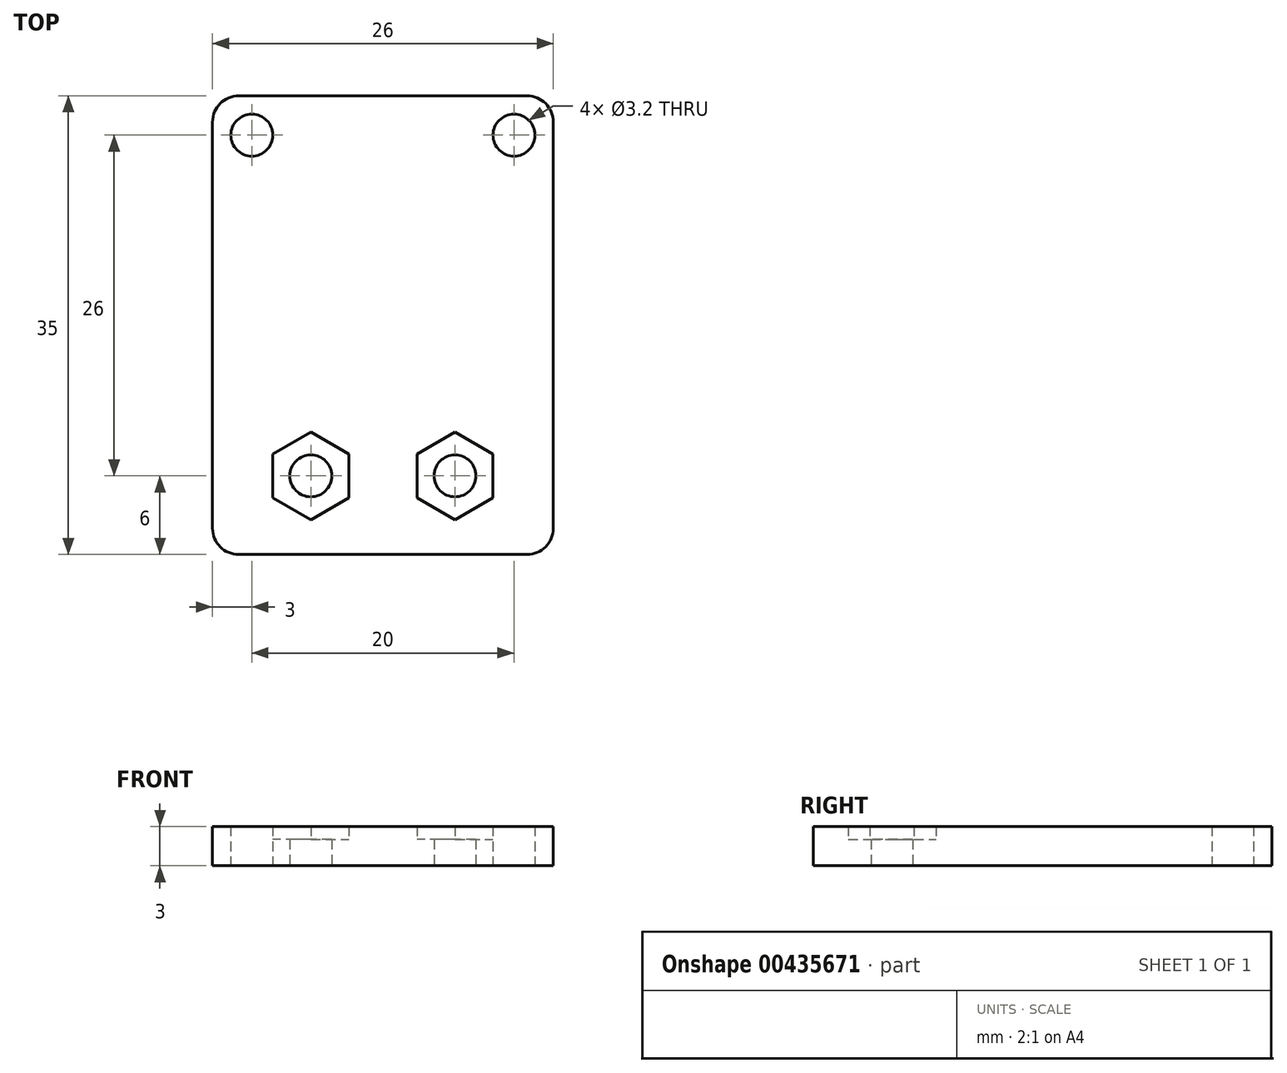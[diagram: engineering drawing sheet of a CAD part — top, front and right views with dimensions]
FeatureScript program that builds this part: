
annotation { "Feature Type Name" : "Feature", "Feature Type Description" : "" }
export const myFeature = defineFeature(function(context is Context, id is Id, definition is map)
    precondition{}
    {
        {
            var Q0;
            Q0=qCreatedBy(makeId("Top.planeOp"),FACE);
            var sketch = newSketch(context, id + "F0", { "sketchPlane" : qUnion([Q0])});
            skLineSegment(sketch, "E0.bottom", {"start": v(2, 0) * mm, "end": v(24, 0) * mm});
            skLineSegment(sketch, "E0.top", {"start": v(2, 35) * mm, "end": v(24, 35) * mm});
            skLineSegment(sketch, "E0.left", {"start": v(0, 2) * mm, "end": v(0, 33) * mm});
            skLineSegment(sketch, "E0.right", {"start": v(26, 2) * mm, "end": v(26, 33) * mm});
            skCircle(sketch, "E1", {"center": v(3, 32) * mm, "radius": 1.6 * mm});
            skCircle(sketch, "E2", {"center": v(23, 32) * mm, "radius": 1.6 * mm});
            skCircle(sketch, "E3", {"center": v(7.5, 6) * mm, "radius": 1.6 * mm});
            skCircle(sketch, "E4", {"center": v(18.5, 6) * mm, "radius": 1.6 * mm});
            skPoint(sketch, "E5.visualSharp", {"position": v(0, 35) * mm});
            skArc(sketch, "E5.filletArc", {"start": v(2, 35) * mm, "mid": v(0.59, 34.41) * mm, "end": v(0, 33) * mm});
            skPoint(sketch, "E6.visualSharp", {"position": v(26, 35) * mm});
            skArc(sketch, "E6.filletArc", {"start": v(26, 33) * mm, "mid": v(25.41, 34.41) * mm, "end": v(24, 35) * mm});
            skPoint(sketch, "E7.visualSharp", {"position": v(26, 0) * mm});
            skArc(sketch, "E7.filletArc", {"start": v(24, 0) * mm, "mid": v(25.41, 0.59) * mm, "end": v(26, 2) * mm});
            skPoint(sketch, "E8.visualSharp", {"position": v(0, 0) * mm});
            skArc(sketch, "E8.filletArc", {"start": v(0, 2) * mm, "mid": v(0.59, 0.59) * mm, "end": v(2, 0) * mm});
            skCircle(sketch, "E9.cCircle", {"center": v(7.5, 6) * mm, "radius": 2.9 * mm, "construction": true});
            skLineSegment(sketch, "E9.0", {"start": v(4.6, 4.33) * mm, "end": v(4.6, 7.67) * mm});
            skLineSegment(sketch, "E9.1", {"start": v(4.6, 7.67) * mm, "end": v(7.5, 9.35) * mm});
            skLineSegment(sketch, "E9.2", {"start": v(7.5, 9.35) * mm, "end": v(10.4, 7.67) * mm});
            skLineSegment(sketch, "E9.3", {"start": v(10.4, 7.67) * mm, "end": v(10.4, 4.33) * mm});
            skLineSegment(sketch, "E9.4", {"start": v(10.4, 4.33) * mm, "end": v(7.5, 2.65) * mm});
            skLineSegment(sketch, "E9.5", {"start": v(7.5, 2.65) * mm, "end": v(4.6, 4.33) * mm});
            skPoint(sketch, "E9.0.midPoint", {"position": v(4.6, 6) * mm});
            skCircle(sketch, "E10.cCircle", {"center": v(18.5, 6) * mm, "radius": 2.9 * mm, "construction": true});
            skLineSegment(sketch, "E10.0", {"start": v(15.6, 4.33) * mm, "end": v(15.6, 7.67) * mm});
            skLineSegment(sketch, "E10.1", {"start": v(15.6, 7.67) * mm, "end": v(18.5, 9.35) * mm});
            skLineSegment(sketch, "E10.2", {"start": v(18.5, 9.35) * mm, "end": v(21.4, 7.67) * mm});
            skLineSegment(sketch, "E10.3", {"start": v(21.4, 7.67) * mm, "end": v(21.4, 4.33) * mm});
            skLineSegment(sketch, "E10.4", {"start": v(21.4, 4.33) * mm, "end": v(18.5, 2.65) * mm});
            skLineSegment(sketch, "E10.5", {"start": v(18.5, 2.65) * mm, "end": v(15.6, 4.33) * mm});
            skPoint(sketch, "E10.0.midPoint", {"position": v(15.6, 6) * mm});
            skSolve(sketch);
        }
        {
            var Q0;
            Q0=makeQuery(id+"F0.imprint","IMPRINT",FACE,{"disambiguationData":[TD([[makeQuery(id+"F0.imprint","IMPRINT",EDGE,{"derivedFrom":sQuery(id+"F0.wireOp",EDGE,"E0.bottom")}),1.0]])]});
            extrude(context, id + "F1", {"entities" : qUnion([Q0]), "depth" : 3 * mm});
        }
        {
            var Q0;
            Q0=makeQuery(id+"F0.imprint","IMPRINT",FACE,{"disambiguationData":[TD([[makeQuery(id+"F0.imprint","IMPRINT",EDGE,{"derivedFrom":sQuery(id+"F0.wireOp",EDGE,"E3")}),-1.0]])]});
            var Q1;
            Q1=makeQuery(id+"F0.imprint","IMPRINT",FACE,{"disambiguationData":[TD([[makeQuery(id+"F0.imprint","IMPRINT",EDGE,{"derivedFrom":sQuery(id+"F0.wireOp",EDGE,"E4")}),-1.0]])]});
            extrude(context, id + "F2", {"entities" : qUnion([Q0, Q1]), "operationType" : NewBodyOperationType.ADD, "depth" : 2 * mm});
        }
    });
